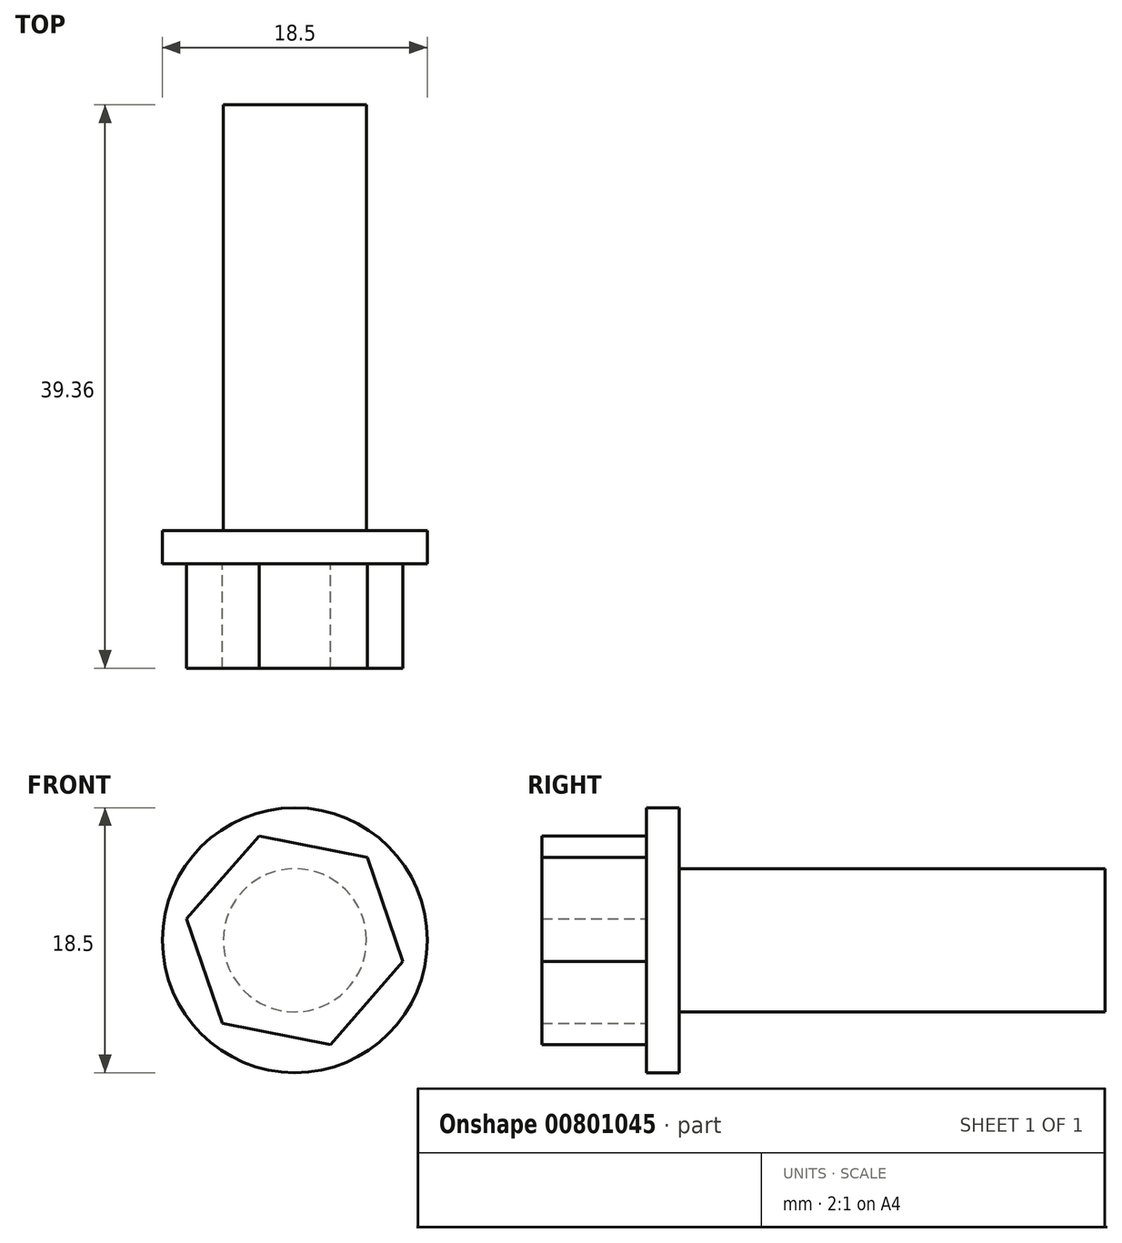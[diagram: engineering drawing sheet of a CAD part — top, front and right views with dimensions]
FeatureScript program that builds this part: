
annotation { "Feature Type Name" : "Feature", "Feature Type Description" : "" }
export const myFeature = defineFeature(function(context is Context, id is Id, definition is map)
    precondition{}
    {
        {
            var Q0;
            Q0=qCreatedBy(makeId("Front.planeOp"),FACE);
            var sketch = newSketch(context, id + "F0", { "sketchPlane" : qUnion([Q0])});
            skCircle(sketch, "E0", {"center": v(0, 0) * mm, "radius": 5 * mm});
            skSolve(sketch);
        }
        {
            var Q0;
            Q0 = qSketchRegion(id + "F0", true);
            extrude(context, id + "F1", {"entities" : qUnion([Q0]), "depth" : 29.76 * mm, "offsetDistance" : 25 * mm});
        }
        {
            var Q0;
            Q0=makeQuery(id+"F1.opExtrude","CAP_FACE",FACE,{"disambiguationData":[OSD([sQuery(id+"F0.wireOp",EDGE,"E0")])],"isStart":false});
            cPlane(context, id + "F2", {"entities" : qUnion([Q0]), "cplaneType" : CPlaneType.OFFSET, "offset" : 0 * mm, "width" : 150 * mm, "height" : 150 * mm});
        }
        {
            var Q0;
            Q0=qCreatedBy(id+"F2.planeOp",FACE);
            var sketch = newSketch(context, id + "F3", { "sketchPlane" : qUnion([Q0])});
            skCircle(sketch, "E1", {"center": v(0, 0) * mm, "radius": 9.25 * mm});
            skSolve(sketch);
        }
        {
            var Q0;
            Q0=makeQuery(id+"F3.imprint","IMPRINT",FACE,{"disambiguationData":[TD([[makeQuery(id+"F3.imprint","IMPRINT",EDGE,{"derivedFrom":sQuery(id+"F3.wireOp",EDGE,"E1")}),1.0]])]});
            extrude(context, id + "F4", {"entities" : qUnion([Q0]), "operationType" : NewBodyOperationType.ADD, "depth" : 2.3 * mm, "offsetDistance" : 25 * mm});
        }
        {
            var Q0;
            Q0=makeQuery(id+"F4.opExtrude","CAP_FACE",FACE,{"disambiguationData":[OSD([sQuery(id+"F3.wireOp",EDGE,"E1")])],"isStart":false});
            cPlane(context, id + "F5", {"entities" : qUnion([Q0]), "cplaneType" : CPlaneType.OFFSET, "offset" : 0 * mm, "width" : 150 * mm, "height" : 150 * mm});
        }
        {
            var Q0;
            Q0=qCreatedBy(id+"F5.planeOp",FACE);
            var sketch = newSketch(context, id + "F6", { "sketchPlane" : qUnion([Q0])});
            skCircle(sketch, "E2", {"center": v(0, 0) * mm, "radius": 7.7 * mm});
            skCircle(sketch, "E3.cCircle", {"center": v(0, 0) * mm, "radius": 7.7 * mm, "construction": true});
            skLineSegment(sketch, "E3.0", {"start": v(5.07, 5.8) * mm, "end": v(7.55, -1.49) * mm});
            skLineSegment(sketch, "E3.1", {"start": v(7.55, -1.49) * mm, "end": v(2.49, -7.29) * mm});
            skLineSegment(sketch, "E3.2", {"start": v(2.49, -7.29) * mm, "end": v(-5.07, -5.8) * mm});
            skLineSegment(sketch, "E3.3", {"start": v(-5.07, -5.8) * mm, "end": v(-7.55, 1.49) * mm});
            skLineSegment(sketch, "E3.4", {"start": v(-7.55, 1.49) * mm, "end": v(-2.49, 7.29) * mm});
            skLineSegment(sketch, "E3.5", {"start": v(-2.49, 7.29) * mm, "end": v(5.07, 5.8) * mm});
            skSolve(sketch);
        }
        {
            var Q0;
            Q0=makeQuery(id+"F6.imprint","IMPRINT",FACE,{"disambiguationData":[TD([[makeQuery(id+"F6.imprint","IMPRINT",EDGE,{"derivedFrom":sQuery(id+"F6.wireOp",EDGE,"E3.0")}),-1.0]])]});
            extrude(context, id + "F7", {"entities" : qUnion([Q0]), "operationType" : NewBodyOperationType.ADD, "depth" : 7.3 * mm, "offsetDistance" : 25 * mm});
        }
    });
